# Revit family: Toilet_Seat-Elongated_Closed_Front-KALLISTA-Modern-P70363
name_source: partatom
category: Specialty Equipment
units: mm (PartAtom-declared; Revit-internal decimal feet)

## family parameters
Cut with Voids When Loaded = No
Host = Face
Maintain Annotation Orientation = No
OmniClass Number = 23.31.25.00
OmniClass Title = Toilet and Bath Specialties
Part Type = Normal
Room Calculation Point = No
Round Connector Dimension = Use Diameter
Shared = No

## types (1)
- 0-White
    ADA Compliant = No
    Assembly Code = C1030200
    Date Modified = 06/13/2025
    Default Elevation = 42"
    Description = Toilet Seat with Slow Close, Quick Hinge Release
    Finish = Kallista-Plastic-0-White
    Height = 2 1/16"
    Length = 18 5/8"
    Manufacturer = Kallista Co.
    Master Format 2014 = 10 28 00
    Master Format 2014 Name = Toilet, Bath, and Laundry Accessories
    Material = Plastic
    Model = P70363-00-0
    Product Documentation Link = https://techcomm.kohler.com
    Product Name = Modern
    Product Page URL = https://www.kallista.com
    Type = 1
    URL = https://www.kallista.com
    WaterSense Certified = No
    Width = 14 3/16"

## geometry (parser evidence)
native form markers: Sweep x6
no freeform markers — native parametric forms only
